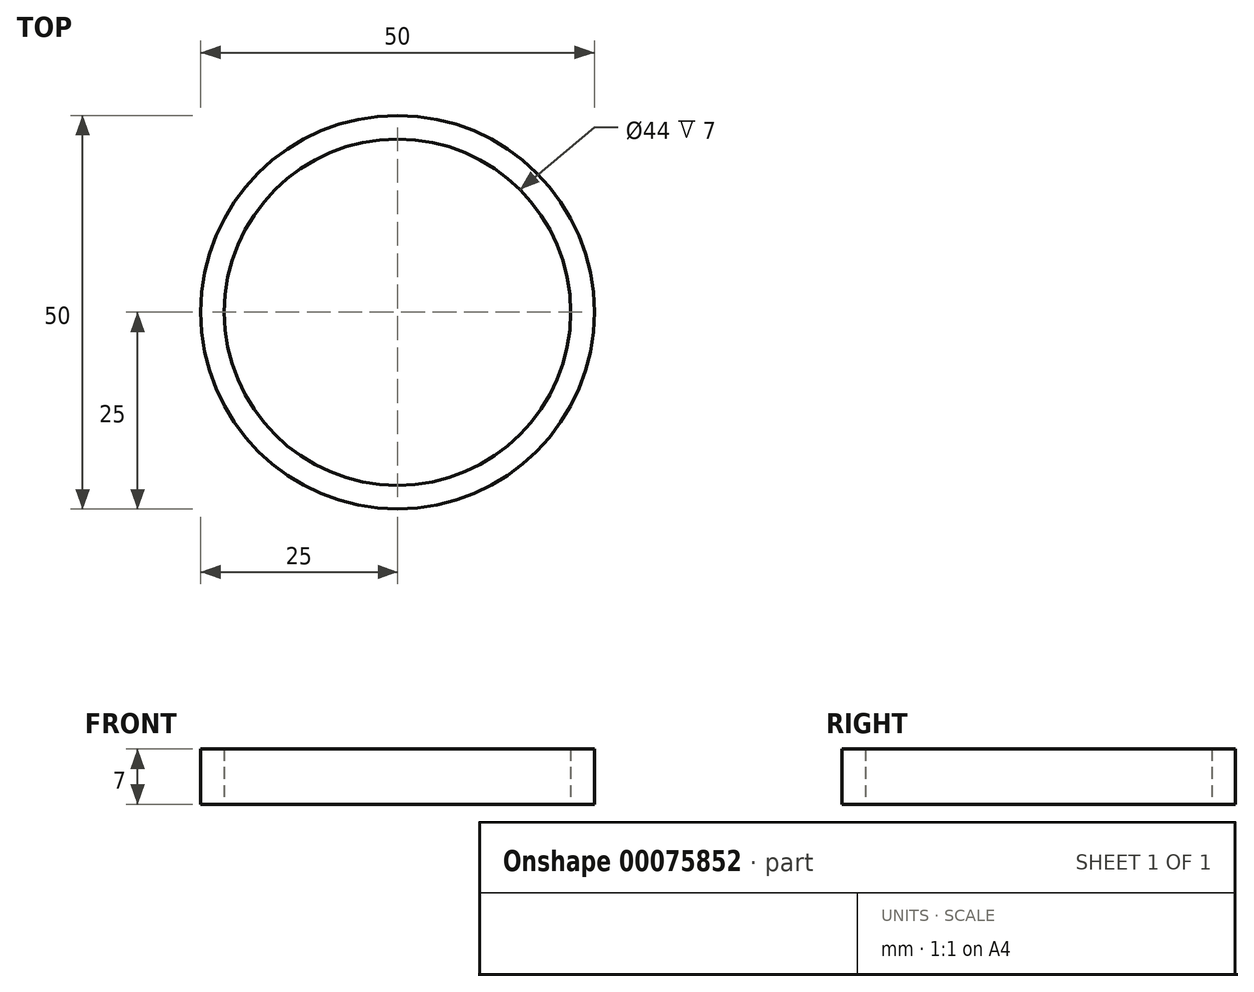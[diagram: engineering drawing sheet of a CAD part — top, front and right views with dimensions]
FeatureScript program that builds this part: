
annotation { "Feature Type Name" : "Feature", "Feature Type Description" : "" }
export const myFeature = defineFeature(function(context is Context, id is Id, definition is map)
    precondition{}
    {
        {
            var Q0;
            Q0=qCreatedBy(makeId("Top.planeOp"),FACE);
            var sketch = newSketch(context, id + "F0", { "sketchPlane" : qUnion([Q0])});
            skCircle(sketch, "E0", {"center": v(0, 0) * mm, "radius": 25 * mm});
            skCircle(sketch, "E1", {"center": v(0, 0) * mm, "radius": 22 * mm});
            skSolve(sketch);
        }
        {
            var Q0;
            Q0=makeQuery(id+"F0.imprint","IMPRINT",FACE,{"disambiguationData":[TD([[makeQuery(id+"F0.imprint","IMPRINT",EDGE,{"derivedFrom":sQuery(id+"F0.wireOp",EDGE,"E0")}),1.0]])]});
            extrude(context, id + "F1", {"entities" : qUnion([Q0]), "depth" : 7 * mm});
        }
    });
